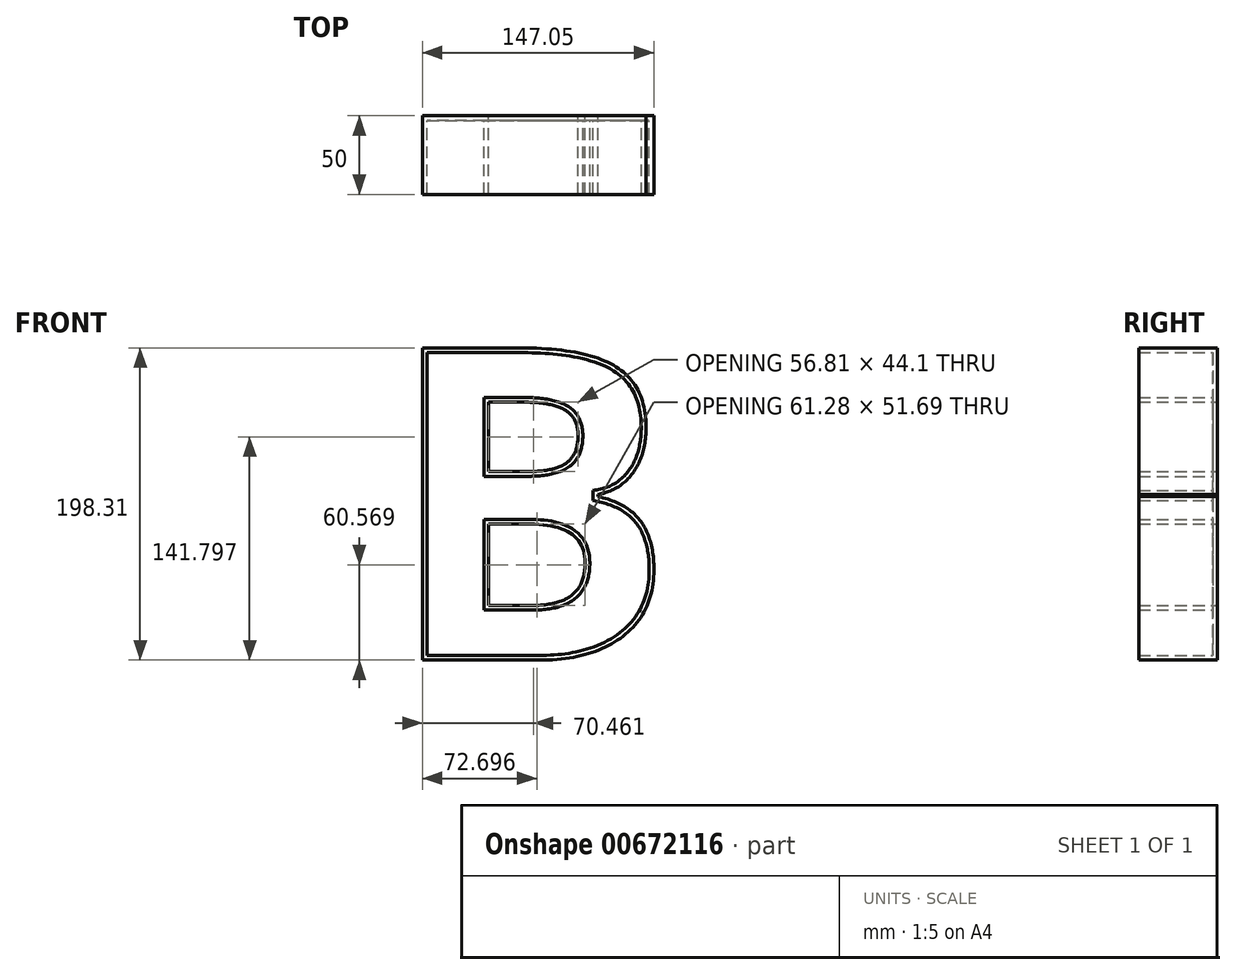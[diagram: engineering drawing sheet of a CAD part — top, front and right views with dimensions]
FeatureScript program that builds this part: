
annotation { "Feature Type Name" : "Feature", "Feature Type Description" : "" }
export const myFeature = defineFeature(function(context is Context, id is Id, definition is map)
    precondition{}
    {
        {
            var Q0;
            Q0=qCreatedBy(makeId("Front.planeOp"),FACE);
            var sketch = newSketch(context, id + "F0", { "sketchPlane" : qUnion([Q0])});
            skText(sketch, "E0", { "text": "B", "fontName": "OpenSans-Bold.ttf"});
            const initialGuessF0  = {"E0": [-0.0961, -0.09654, 1, 0, 0.2]};
            skSetInitialGuess(sketch, initialGuessF0);
            skSolve(sketch);
        }
        {
            var Q0;
            Q0=makeQuery(id+"F0.imprint","IMPRINT",FACE,{"disambiguationData":[TD([[makeQuery(id+"F0.imprint","IMPRINT",EDGE,{"derivedFrom":sQuery(id+"F0.wireOp",EDGE,"E0.sketch_text.stroke-0")}),-1.0]])]});
            extrude(context, id + "F1", {"entities" : qUnion([Q0]), "depth" : 50 * mm, "offsetDistance" : 25 * mm});
        }
        {
            var Q0;
            Q0=makeQuery(id+"F1.opExtrude","CAP_FACE",FACE,{"disambiguationData":[OSD([sQuery(id+"F0.wireOp",EDGE,"E0.sketch_text.stroke-0"),sQuery(id+"F0.wireOp",EDGE,"E0.sketch_text.stroke-1"),sQuery(id+"F0.wireOp",EDGE,"E0.sketch_text.stroke-2"),sQuery(id+"F0.wireOp",EDGE,"E0.sketch_text.stroke-3"),sQuery(id+"F0.wireOp",EDGE,"E0.sketch_text.stroke-4"),sQuery(id+"F0.wireOp",EDGE,"E0.sketch_text.stroke-5"),sQuery(id+"F0.wireOp",EDGE,"E0.sketch_text.stroke-6"),sQuery(id+"F0.wireOp",EDGE,"E0.sketch_text.stroke-7"),sQuery(id+"F0.wireOp",EDGE,"E0.sketch_text.stroke-8"),sQuery(id+"F0.wireOp",EDGE,"E0.sketch_text.stroke-9"),sQuery(id+"F0.wireOp",EDGE,"E0.sketch_text.stroke-10"),sQuery(id+"F0.wireOp",EDGE,"E0.sketch_text.stroke-11"),sQuery(id+"F0.wireOp",EDGE,"E0.sketch_text.stroke-12"),sQuery(id+"F0.wireOp",EDGE,"E0.sketch_text.stroke-13"),sQuery(id+"F0.wireOp",EDGE,"E0.sketch_text.stroke-14"),sQuery(id+"F0.wireOp",EDGE,"E0.sketch_text.stroke-15"),sQuery(id+"F0.wireOp",EDGE,"E0.sketch_text.stroke-16"),sQuery(id+"F0.wireOp",EDGE,"E0.sketch_text.stroke-17"),sQuery(id+"F0.wireOp",EDGE,"E0.sketch_text.stroke-18"),sQuery(id+"F0.wireOp",EDGE,"E0.sketch_text.stroke-19"),sQuery(id+"F0.wireOp",EDGE,"E0.sketch_text.stroke-20"),sQuery(id+"F0.wireOp",EDGE,"E0.sketch_text.stroke-21"),sQuery(id+"F0.wireOp",EDGE,"E0.sketch_text.stroke-22"),sQuery(id+"F0.wireOp",EDGE,"E0.sketch_text.stroke-23"),sQuery(id+"F0.wireOp",EDGE,"E0.sketch_text.stroke-24")])],"isStart":false});
            shell(context, id + "F2", {"entities" : qUnion([Q0]), "thickness" : 3 * mm});
        }
    });
